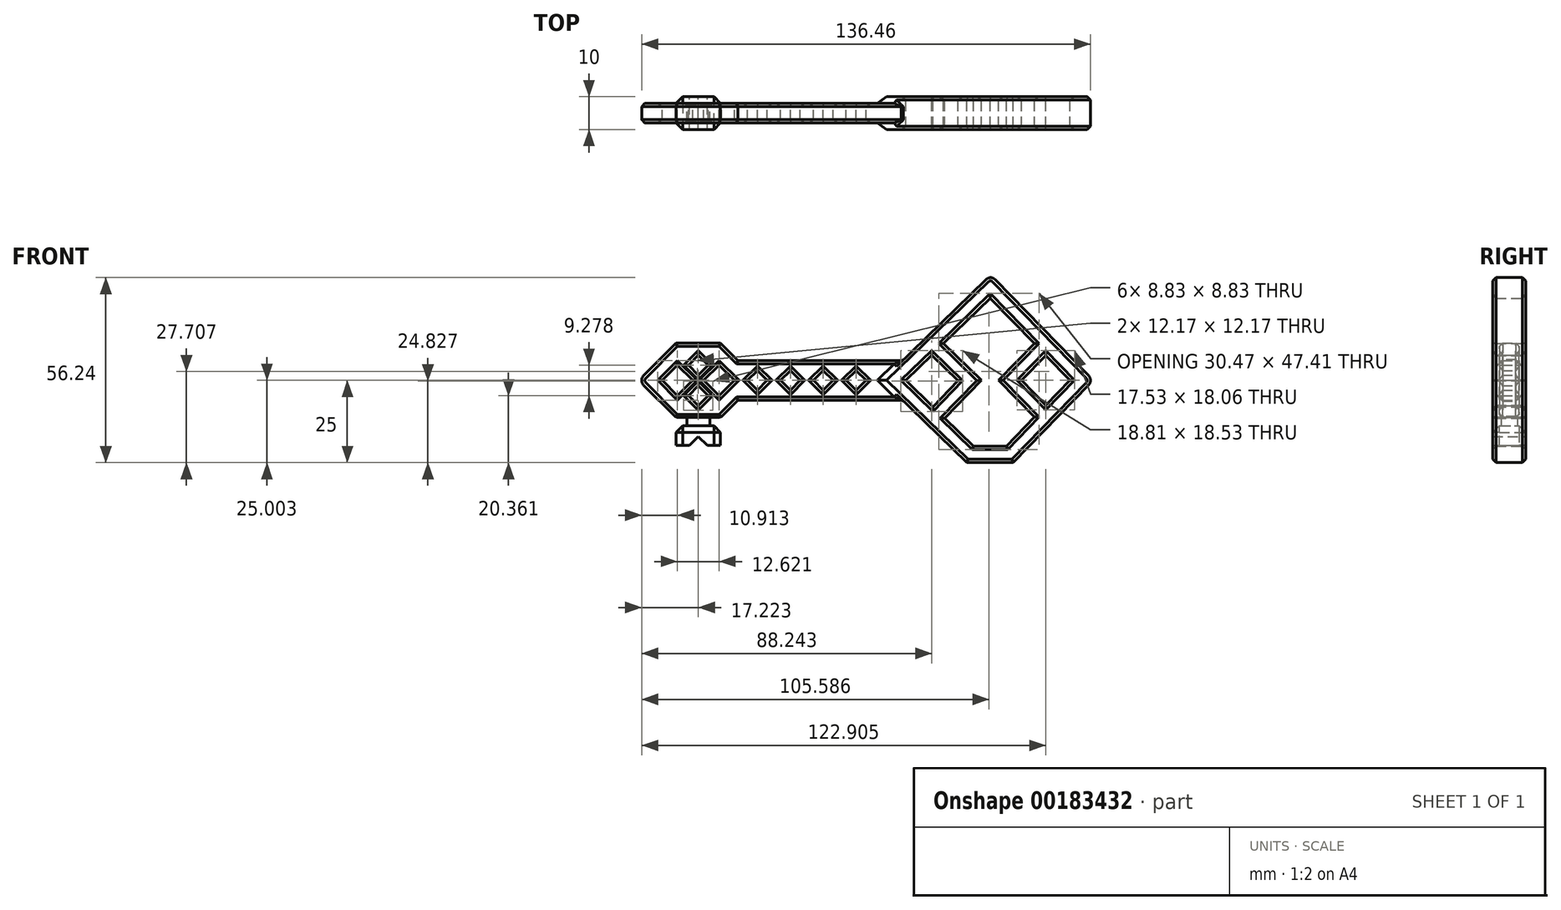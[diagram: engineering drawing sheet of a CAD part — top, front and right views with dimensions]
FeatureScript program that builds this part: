
annotation { "Feature Type Name" : "Feature", "Feature Type Description" : "" }
export const myFeature = defineFeature(function(context is Context, id is Id, definition is map)
    precondition{}
    {
        {
            var Q0;
            Q0=qCreatedBy(makeId("Front.planeOp"),FACE);
            var sketch = newSketch(context, id + "F0", { "sketchPlane" : qUnion([Q0])});
            skLineSegment(sketch, "E0", {"start": v(20.1, -6) * mm, "end": v(-29.9, -6) * mm});
            skLineSegment(sketch, "E1.MirrorCS", {"start": v(20.1, 6) * mm, "end": v(-29.9, 6) * mm});
            skLineSegment(sketch, "E2", {"start": v(71.1, 0) * mm, "end": v(63.73, 7.6) * mm});
            skLineSegment(sketch, "E3", {"start": v(46.84, 25) * mm, "end": v(32.62, 11.18) * mm});
            skLineSegment(sketch, "E4", {"start": v(21.1, 0) * mm, "end": v(29.37, -8.02) * mm});
            skLineSegment(sketch, "E5", {"start": v(51.7, -20) * mm, "end": v(60.26, -11.18) * mm});
            skLineSegment(sketch, "E6.0", {"start": v(45.51, 30.68) * mm, "end": v(13.93, 0) * mm});
            skLineSegment(sketch, "E6.1", {"start": v(76.72, 1.4) * mm, "end": v(48.34, 30.64) * mm});
            skLineSegment(sketch, "E6.2", {"start": v(53.8, -25) * mm, "end": v(76.72, -1.4) * mm});
            skLineSegment(sketch, "E6.3", {"start": v(13.93, 0) * mm, "end": v(39.67, -25) * mm});
            skLineSegment(sketch, "E7", {"start": v(41.7, -20) * mm, "end": v(51.7, -20) * mm});
            skLineSegment(sketch, "E8", {"start": v(32.95, -11.5) * mm, "end": v(44.13, 0) * mm});
            skLineSegment(sketch, "E9", {"start": v(44.13, 0) * mm, "end": v(32.62, 11.18) * mm});
            skLineSegment(sketch, "E10", {"start": v(60.25, 11.18) * mm, "end": v(49.4, 0) * mm});
            skLineSegment(sketch, "E11", {"start": v(49.4, 0) * mm, "end": v(60.26, -11.18) * mm});
            skLineSegment(sketch, "E12.0", {"start": v(37.06, -0.1) * mm, "end": v(29.03, 7.7) * mm});
            skLineSegment(sketch, "E12.1", {"start": v(29.37, -8.02) * mm, "end": v(37.06, -0.1) * mm});
            skLineSegment(sketch, "E13.0", {"start": v(56.37, 0) * mm, "end": v(63.74, -7.59) * mm});
            skLineSegment(sketch, "E13.1", {"start": v(63.73, 7.6) * mm, "end": v(56.37, 0) * mm});
            skLineSegment(sketch, "E14.trimOffspring", {"start": v(60.25, 11.18) * mm, "end": v(46.84, 25) * mm});
            skLineSegment(sketch, "E15.trimOffspring", {"start": v(63.74, -7.59) * mm, "end": v(71.1, 0) * mm});
            skLineSegment(sketch, "E16.trimOffspring", {"start": v(32.95, -11.5) * mm, "end": v(41.7, -20) * mm});
            skLineSegment(sketch, "E17.trimOffspring", {"start": v(29.03, 7.7) * mm, "end": v(21.1, 0) * mm});
            skLineSegment(sketch, "E18", {"start": v(39.67, -25) * mm, "end": v(53.8, -25) * mm});
            skPoint(sketch, "E19.orphan", {"position": v(46.84, -25) * mm});
            skPoint(sketch, "E20.visualSharp", {"position": v(46.95, 32.07) * mm});
            skArc(sketch, "E20.filletArc", {"start": v(48.34, 30.64) * mm, "mid": v(46.93, 31.24) * mm, "end": v(45.51, 30.68) * mm});
            skPoint(sketch, "E21.visualSharp", {"position": v(78.07, 0) * mm});
            skArc(sketch, "E21.filletArc", {"start": v(76.72, -1.4) * mm, "mid": v(77.29, 0) * mm, "end": v(76.72, 1.4) * mm});
            skLineSegment(sketch, "E22", {"start": v(-35.2, 11.31) * mm, "end": v(-48.69, 11.31) * mm});
            skLineSegment(sketch, "E23", {"start": v(-48.69, 11.31) * mm, "end": v(-58.59, 1.41) * mm});
            skLineSegment(sketch, "E24", {"start": v(-29.9, 6) * mm, "end": v(-35.2, 11.31) * mm});
            skLineSegment(sketch, "E25", {"start": v(-29.9, -6) * mm, "end": v(-35.2, -11.31) * mm});
            skLineSegment(sketch, "E26", {"start": v(-35.2, -11.31) * mm, "end": v(-48.69, -11.31) * mm});
            skLineSegment(sketch, "E27", {"start": v(-48.69, -11.31) * mm, "end": v(-58.59, -1.41) * mm});
            skLineSegment(sketch, "E28", {"start": v(-45.45, -11.31) * mm, "end": v(-45.45, -13.81) * mm});
            skLineSegment(sketch, "E29", {"start": v(-41.95, -11.31) * mm, "end": v(-41.95, -29.27) * mm, "construction": true});
            skLineSegment(sketch, "E30", {"start": v(-41.95, -13.81) * mm, "end": v(-48.69, -13.81) * mm});
            skLineSegment(sketch, "E31", {"start": v(-48.69, -13.81) * mm, "end": v(-48.69, -19.81) * mm});
            skLineSegment(sketch, "E32", {"start": v(-48.69, -19.81) * mm, "end": v(-44.69, -19.81) * mm});
            skLineSegment(sketch, "E33", {"start": v(-44.69, -19.81) * mm, "end": v(-41.95, -17.07) * mm});
            skLineSegment(sketch, "E34.MirrorCS", {"start": v(-38.45, -11.31) * mm, "end": v(-38.45, -13.81) * mm});
            skLineSegment(sketch, "E35.MirrorCS", {"start": v(-41.95, -13.81) * mm, "end": v(-35.2, -13.81) * mm});
            skLineSegment(sketch, "E36.MirrorCS", {"start": v(-35.2, -13.81) * mm, "end": v(-35.2, -19.81) * mm});
            skLineSegment(sketch, "E37.MirrorCS", {"start": v(-35.2, -19.81) * mm, "end": v(-39.2, -19.81) * mm});
            skLineSegment(sketch, "E38.MirrorCS", {"start": v(-39.2, -19.81) * mm, "end": v(-41.95, -17.07) * mm});
            skLineSegment(sketch, "E39.0", {"start": v(-33.43, -2.46) * mm, "end": v(-35.64, -4.67) * mm});
            skLineSegment(sketch, "E39.2", {"start": v(-33.43, 2.46) * mm, "end": v(-35.64, 4.67) * mm});
            skLineSegment(sketch, "E39.4", {"start": v(-48.26, 4.67) * mm, "end": v(-52.93, 0) * mm});
            skLineSegment(sketch, "E39.5", {"start": v(-48.26, -4.67) * mm, "end": v(-52.93, 0) * mm});
            skLineSegment(sketch, "E40.trimOffspring", {"start": v(-43.59, 0) * mm, "end": v(-48.26, -4.67) * mm});
            skLineSegment(sketch, "E41.trimOffspring", {"start": v(-43.59, 0) * mm, "end": v(-48.26, 4.67) * mm});
            skLineSegment(sketch, "E42.trimOffspring", {"start": v(-40.3, 0) * mm, "end": v(-35.64, 4.67) * mm});
            skLineSegment(sketch, "E43.trimOffspring", {"start": v(-40.3, 0) * mm, "end": v(-35.64, -4.67) * mm});
            skLineSegment(sketch, "E44", {"start": v(-33.43, 2.46) * mm, "end": v(-30.96, 0) * mm});
            skLineSegment(sketch, "E45", {"start": v(-30.96, 0) * mm, "end": v(-33.43, -2.46) * mm});
            skPoint(sketch, "E46.visualSharp", {"position": v(-60, 0) * mm});
            skArc(sketch, "E46.filletArc", {"start": v(-58.59, 1.41) * mm, "mid": v(-59.17, 0) * mm, "end": v(-58.59, -1.41) * mm});
            skLineSegment(sketch, "E47", {"start": v(-26.96, 0) * mm, "end": v(-23.96, 3) * mm});
            skLineSegment(sketch, "E48", {"start": v(-23.96, 3) * mm, "end": v(-20.96, 0) * mm});
            skLineSegment(sketch, "E49.1.0.0", {"start": v(-16.96, 0) * mm, "end": v(-13.96, 3) * mm});
            skLineSegment(sketch, "E49.1.0.1", {"start": v(-13.96, 3) * mm, "end": v(-10.96, 0) * mm});
            skLineSegment(sketch, "E49.2.0.0", {"start": v(-6.96, 0) * mm, "end": v(-3.96, 3) * mm});
            skLineSegment(sketch, "E49.2.0.1", {"start": v(-3.96, 3) * mm, "end": v(-0.96, 0) * mm});
            skLineSegment(sketch, "E49.3.0.0", {"start": v(3.04, 0) * mm, "end": v(6.04, 3) * mm});
            skLineSegment(sketch, "E49.3.0.1", {"start": v(6.04, 3) * mm, "end": v(9.04, 0) * mm});
            skLineSegment(sketch, "E49.direction1", {"start": v(-26.96, 0) * mm, "end": v(-16.96, 0) * mm, "construction": true});
            skLineSegment(sketch, "E50.MirrorCS", {"start": v(-26.96, 0) * mm, "end": v(-23.96, -3) * mm});
            skLineSegment(sketch, "E51.MirrorCS", {"start": v(-23.96, -3) * mm, "end": v(-20.96, 0) * mm});
            skLineSegment(sketch, "E52.MirrorCS", {"start": v(-16.96, 0) * mm, "end": v(-13.96, -3) * mm});
            skLineSegment(sketch, "E53.MirrorCS", {"start": v(-13.96, -3) * mm, "end": v(-10.96, 0) * mm});
            skLineSegment(sketch, "E54.MirrorCS", {"start": v(-6.96, 0) * mm, "end": v(-3.96, -3) * mm});
            skLineSegment(sketch, "E55.MirrorCS", {"start": v(-3.96, -3) * mm, "end": v(-0.96, 0) * mm});
            skLineSegment(sketch, "E56.MirrorCS", {"start": v(3.04, 0) * mm, "end": v(6.04, -3) * mm});
            skLineSegment(sketch, "E57.MirrorCS", {"start": v(6.04, -3) * mm, "end": v(9.04, 0) * mm});
            skLineSegment(sketch, "E58.1.0.0", {"start": v(-44.95, -4.64) * mm, "end": v(-41.95, -1.64) * mm});
            skLineSegment(sketch, "E58.1.0.1", {"start": v(-41.95, -1.64) * mm, "end": v(-38.95, -4.64) * mm});
            skLineSegment(sketch, "E59.MirrorCS", {"start": v(-44.95, -4.64) * mm, "end": v(-41.95, -7.64) * mm});
            skLineSegment(sketch, "E60.MirrorCS", {"start": v(-41.95, -7.64) * mm, "end": v(-38.95, -4.64) * mm});
            skLineSegment(sketch, "E61", {"start": v(-41.95, 20.91) * mm, "end": v(-41.95, -13.81) * mm, "construction": true});
            skLineSegment(sketch, "E62.MirrorCS", {"start": v(-44.95, 4.64) * mm, "end": v(-41.95, 1.64) * mm});
            skLineSegment(sketch, "E63.MirrorCS", {"start": v(-41.95, 1.64) * mm, "end": v(-38.95, 4.64) * mm});
            skLineSegment(sketch, "E64.MirrorCS", {"start": v(-41.95, 7.64) * mm, "end": v(-38.95, 4.64) * mm});
            skLineSegment(sketch, "E65.MirrorCS", {"start": v(-44.95, 4.64) * mm, "end": v(-41.95, 7.64) * mm});
            skSolve(sketch);
        }
        {
            var Q0;
            Q0=makeQuery(id+"F0.imprint","IMPRINT",FACE,{"disambiguationData":[TD([[makeQuery(id+"F0.imprint","IMPRINT",EDGE,{"derivedFrom":sQuery(id+"F0.wireOp",EDGE,"E2")}),-1.0]])]});
            var Q1;
            {var subQ0=sQuery(id+"F0.wireOp",EDGE,"E31");Q1=makeQuery(id+"F0.imprint","IMPRINT",FACE,{"disambiguationData":[TD([[makeQuery(id+"F0.imprint","IMPRINT",EDGE,{"derivedFrom":subQ0}),1.0]])]});}
            extrude(context, id + "F1", {"entities" : qUnion([Q0, Q1]), "endBound" : BoundingType.SYMMETRIC, "depth" : 10 * mm});
        }
        {
            var Q0;
            {var subQ4=sQuery(id+"F0.wireOp",EDGE,"E0");Q0=makeQuery(id+"F0.imprint","IMPRINT",FACE,{"disambiguationData":[TD([[makeQuery(id+"F0.imprint","IMPRINT",EDGE,{"derivedFrom":subQ4}),-1.0]])]});}
            var Q1;
            Q1=makeQuery(id+"F0.imprint","IMPRINT",FACE,{"disambiguationData":[TD([[makeQuery(id+"F0.imprint","IMPRINT",EDGE,{"derivedFrom":sQuery(id+"F0.wireOp",EDGE,"E39.3")}),1.0]])]});
            var Q2;
            Q2=makeQuery(id+"F0.imprint","IMPRINT",FACE,{"disambiguationData":[TD([[makeQuery(id+"F0.imprint","IMPRINT",EDGE,{"derivedFrom":sQuery(id+"F0.wireOp",EDGE,"E39.1")}),-1.0]])]});
            extrude(context, id + "F2", {"entities" : qUnion([Q0, Q1, Q2]), "operationType" : NewBodyOperationType.ADD, "endBound" : BoundingType.SYMMETRIC, "depth" : 6 * mm});
        }
        {
            var Q0;
            {var subQ2=sQuery(id+"F0.wireOp",EDGE,"E28");Q0=makeQuery(id+"F0.imprint","IMPRINT",FACE,{"disambiguationData":[TD([[makeQuery(id+"F0.imprint","IMPRINT",EDGE,{"derivedFrom":subQ2}),1.0]])]});}
            extrude(context, id + "F3", {"entities" : qUnion([Q0]), "endBound" : BoundingType.SYMMETRIC, "depth" : 5 * mm});
        }
        {
            var Q0;
            Q0=makeQuery(id+"F2.opExtrude","CAP_EDGE",EDGE,{"disambiguationData":[OSD([sQuery(id+"F0.wireOp",EDGE,"E47")])],"isStart":false});
            var Q1;
            Q1=makeQuery(id+"F2.opExtrude","CAP_EDGE",EDGE,{"disambiguationData":[OSD([sQuery(id+"F0.wireOp",EDGE,"E48")])],"isStart":false});
            var Q2;
            Q2=makeQuery(id+"F2.opExtrude","CAP_EDGE",EDGE,{"disambiguationData":[OSD([sQuery(id+"F0.wireOp",EDGE,"E51.MirrorCS")])],"isStart":false});
            var Q3;
            Q3=makeQuery(id+"F2.opExtrude","CAP_EDGE",EDGE,{"disambiguationData":[OSD([sQuery(id+"F0.wireOp",EDGE,"E50.MirrorCS")])],"isStart":false});
            var Q4;
            Q4=makeQuery(id+"F2.opExtrude","CAP_EDGE",EDGE,{"disambiguationData":[OSD([sQuery(id+"F0.wireOp",EDGE,"E49.1.0.0")])],"isStart":false});
            var Q5;
            Q5=makeQuery(id+"F2.opExtrude","CAP_EDGE",EDGE,{"disambiguationData":[OSD([sQuery(id+"F0.wireOp",EDGE,"E49.1.0.1")])],"isStart":false});
            var Q6;
            Q6=makeQuery(id+"F2.opExtrude","CAP_EDGE",EDGE,{"disambiguationData":[OSD([sQuery(id+"F0.wireOp",EDGE,"E53.MirrorCS")])],"isStart":false});
            var Q7;
            Q7=makeQuery(id+"F2.opExtrude","CAP_FACE",FACE,{"disambiguationData":[OSD([sQuery(id+"F0.wireOp",EDGE,"E0"),sQuery(id+"F0.wireOp",EDGE,"E1.MirrorCS"),sQuery(id+"F0.wireOp",EDGE,"E6.0"),sQuery(id+"F0.wireOp",EDGE,"E6.3"),sQuery(id+"F0.wireOp",EDGE,"E22"),sQuery(id+"F0.wireOp",EDGE,"E23"),sQuery(id+"F0.wireOp",EDGE,"E24"),sQuery(id+"F0.wireOp",EDGE,"E25"),sQuery(id+"F0.wireOp",EDGE,"E26"),sQuery(id+"F0.wireOp",EDGE,"E27"),sQuery(id+"F0.wireOp",EDGE,"E39.0"),sQuery(id+"F0.wireOp",EDGE,"E39.1"),sQuery(id+"F0.wireOp",EDGE,"E39.2"),sQuery(id+"F0.wireOp",EDGE,"E39.3"),sQuery(id+"F0.wireOp",EDGE,"E39.4"),sQuery(id+"F0.wireOp",EDGE,"E39.5"),sQuery(id+"F0.wireOp",EDGE,"SuCAYquI-ejI9-Igzf-Qkme-vMYG3JWezhbn"),sQuery(id+"F0.wireOp",EDGE,"5v7E9WHn-bbCv-sJz2-O0Js-mJgPAPqvvkll"),sQuery(id+"F0.wireOp",EDGE,"vqwsvxok-3IlO-Vk3z-uLZy-tBUQALx8QQG8"),sQuery(id+"F0.wireOp",EDGE,"VJvgWDCh-3OEa-ATRK-sCer-f1ydQRvW1O1d"),sQuery(id+"F0.wireOp",EDGE,"E40.trimOffspring"),sQuery(id+"F0.wireOp",EDGE,"E41.trimOffspring"),sQuery(id+"F0.wireOp",EDGE,"E42.trimOffspring"),sQuery(id+"F0.wireOp",EDGE,"E43.trimOffspring"),sQuery(id+"F0.wireOp",EDGE,"E44"),sQuery(id+"F0.wireOp",EDGE,"E45"),sQuery(id+"F0.wireOp",EDGE,"E46.filletArc"),sQuery(id+"F0.wireOp",EDGE,"E47"),sQuery(id+"F0.wireOp",EDGE,"E48"),sQuery(id+"F0.wireOp",EDGE,"E49.1.0.0"),sQuery(id+"F0.wireOp",EDGE,"E49.1.0.1"),sQuery(id+"F0.wireOp",EDGE,"E49.2.0.0"),sQuery(id+"F0.wireOp",EDGE,"E49.2.0.1"),sQuery(id+"F0.wireOp",EDGE,"E49.3.0.0"),sQuery(id+"F0.wireOp",EDGE,"E49.3.0.1"),sQuery(id+"F0.wireOp",EDGE,"E50.MirrorCS"),sQuery(id+"F0.wireOp",EDGE,"E51.MirrorCS"),sQuery(id+"F0.wireOp",EDGE,"E52.MirrorCS"),sQuery(id+"F0.wireOp",EDGE,"E53.MirrorCS"),sQuery(id+"F0.wireOp",EDGE,"E54.MirrorCS"),sQuery(id+"F0.wireOp",EDGE,"E55.MirrorCS"),sQuery(id+"F0.wireOp",EDGE,"E56.MirrorCS"),sQuery(id+"F0.wireOp",EDGE,"E57.MirrorCS")])],"isStart":false});
            var Q8;
            Q8=makeQuery(id+"F2.opExtrude","CAP_FACE",FACE,{"disambiguationData":[OSD([sQuery(id+"F0.wireOp",EDGE,"E0"),sQuery(id+"F0.wireOp",EDGE,"E1.MirrorCS"),sQuery(id+"F0.wireOp",EDGE,"E6.0"),sQuery(id+"F0.wireOp",EDGE,"E6.3"),sQuery(id+"F0.wireOp",EDGE,"E22"),sQuery(id+"F0.wireOp",EDGE,"E23"),sQuery(id+"F0.wireOp",EDGE,"E24"),sQuery(id+"F0.wireOp",EDGE,"E25"),sQuery(id+"F0.wireOp",EDGE,"E26"),sQuery(id+"F0.wireOp",EDGE,"E27"),sQuery(id+"F0.wireOp",EDGE,"E39.0"),sQuery(id+"F0.wireOp",EDGE,"E39.1"),sQuery(id+"F0.wireOp",EDGE,"E39.2"),sQuery(id+"F0.wireOp",EDGE,"E39.3"),sQuery(id+"F0.wireOp",EDGE,"E39.4"),sQuery(id+"F0.wireOp",EDGE,"E39.5"),sQuery(id+"F0.wireOp",EDGE,"SuCAYquI-ejI9-Igzf-Qkme-vMYG3JWezhbn"),sQuery(id+"F0.wireOp",EDGE,"5v7E9WHn-bbCv-sJz2-O0Js-mJgPAPqvvkll"),sQuery(id+"F0.wireOp",EDGE,"vqwsvxok-3IlO-Vk3z-uLZy-tBUQALx8QQG8"),sQuery(id+"F0.wireOp",EDGE,"VJvgWDCh-3OEa-ATRK-sCer-f1ydQRvW1O1d"),sQuery(id+"F0.wireOp",EDGE,"E40.trimOffspring"),sQuery(id+"F0.wireOp",EDGE,"E41.trimOffspring"),sQuery(id+"F0.wireOp",EDGE,"E42.trimOffspring"),sQuery(id+"F0.wireOp",EDGE,"E43.trimOffspring"),sQuery(id+"F0.wireOp",EDGE,"E44"),sQuery(id+"F0.wireOp",EDGE,"E45"),sQuery(id+"F0.wireOp",EDGE,"E46.filletArc"),sQuery(id+"F0.wireOp",EDGE,"E47"),sQuery(id+"F0.wireOp",EDGE,"E48"),sQuery(id+"F0.wireOp",EDGE,"E49.1.0.0"),sQuery(id+"F0.wireOp",EDGE,"E49.1.0.1"),sQuery(id+"F0.wireOp",EDGE,"E49.2.0.0"),sQuery(id+"F0.wireOp",EDGE,"E49.2.0.1"),sQuery(id+"F0.wireOp",EDGE,"E49.3.0.0"),sQuery(id+"F0.wireOp",EDGE,"E49.3.0.1"),sQuery(id+"F0.wireOp",EDGE,"E50.MirrorCS"),sQuery(id+"F0.wireOp",EDGE,"E51.MirrorCS"),sQuery(id+"F0.wireOp",EDGE,"E52.MirrorCS"),sQuery(id+"F0.wireOp",EDGE,"E53.MirrorCS"),sQuery(id+"F0.wireOp",EDGE,"E54.MirrorCS"),sQuery(id+"F0.wireOp",EDGE,"E55.MirrorCS"),sQuery(id+"F0.wireOp",EDGE,"E56.MirrorCS"),sQuery(id+"F0.wireOp",EDGE,"E57.MirrorCS")])],"isStart":true});
            var Q9;
            Q9=makeQuery(id+"F2.opExtrude","SWEPT_EDGE",EDGE,{"disambiguationData":[OSD([sQuery(id+"F0.wireOp",EDGE,"E26"),sQuery(id+"F0.wireOp",EDGE,"E27")])]});
            var Q10;
            Q10=makeQuery(id+"F2.opExtrude","SWEPT_EDGE",EDGE,{"disambiguationData":[OSD([sQuery(id+"F0.wireOp",EDGE,"E25"),sQuery(id+"F0.wireOp",EDGE,"E26")])]});
            chamfer(context, id + "F4", {"entities" : qUnion([Q0, Q1, Q2, Q3, Q4, Q5, Q6, Q7, Q8, Q9, Q10]), "width" : 1 * mm, "tangentPropagation" : true});
        }
        {
            var Q0;
            Q0=makeQuery(id+"F1.opExtrude","CAP_EDGE",EDGE,{"disambiguationData":[OSD([sQuery(id+"F0.wireOp",EDGE,"E30"),sQuery(id+"F0.wireOp",EDGE,"E35.MirrorCS")])],"isStart":false});
            var Q1;
            Q1=makeQuery(id+"F1.opExtrude","SWEPT_EDGE",EDGE,{"disambiguationData":[OSD([sQuery(id+"F0.wireOp",EDGE,"E30"),sQuery(id+"F0.wireOp",EDGE,"E31")])]});
            var Q2;
            Q2=makeQuery(id+"F1.opExtrude","SWEPT_EDGE",EDGE,{"disambiguationData":[OSD([sQuery(id+"F0.wireOp",EDGE,"E35.MirrorCS"),sQuery(id+"F0.wireOp",EDGE,"E36.MirrorCS")])]});
            var Q3;
            Q3=makeQuery(id+"F1.opExtrude","CAP_EDGE",EDGE,{"disambiguationData":[OSD([sQuery(id+"F0.wireOp",EDGE,"E30"),sQuery(id+"F0.wireOp",EDGE,"E35.MirrorCS")])],"isStart":true});
            var Q4;
            Q4=makeQuery(id+"F1.opExtrude","CAP_EDGE",EDGE,{"disambiguationData":[OSD([sQuery(id+"F0.wireOp",EDGE,"E31")])],"isStart":false});
            var Q5;
            Q5=makeQuery(id+"F1.opExtrude","CAP_EDGE",EDGE,{"disambiguationData":[OSD([sQuery(id+"F0.wireOp",EDGE,"E36.MirrorCS")])],"isStart":false});
            var Q6;
            Q6=makeQuery(id+"F1.opExtrude","CAP_EDGE",EDGE,{"disambiguationData":[OSD([sQuery(id+"F0.wireOp",EDGE,"E31")])],"isStart":true});
            var Q7;
            Q7=makeQuery(id+"F1.opExtrude","CAP_EDGE",EDGE,{"disambiguationData":[OSD([sQuery(id+"F0.wireOp",EDGE,"E36.MirrorCS")])],"isStart":true});
            chamfer(context, id + "F5", {"entities" : qUnion([Q0, Q1, Q2, Q3, Q4, Q5, Q6, Q7]), "width" : 2 * mm, "tangentPropagation" : true});
        }
        {
            var Q0;
            Q0=makeQuery(id+"F1.opExtrude","CAP_EDGE",EDGE,{"disambiguationData":[OSD([sQuery(id+"F0.wireOp",EDGE,"E12.0")])],"isStart":false});
            var Q1;
            Q1=makeQuery(id+"F1.opExtrude","CAP_EDGE",EDGE,{"disambiguationData":[OSD([sQuery(id+"F0.wireOp",EDGE,"E12.1")])],"isStart":false});
            var Q2;
            Q2=makeQuery(id+"F1.opExtrude","CAP_EDGE",EDGE,{"disambiguationData":[OSD([sQuery(id+"F0.wireOp",EDGE,"E17.trimOffspring")])],"isStart":false});
            var Q3;
            Q3=makeQuery(id+"F1.opExtrude","CAP_EDGE",EDGE,{"disambiguationData":[OSD([sQuery(id+"F0.wireOp",EDGE,"E4")])],"isStart":false});
            var Q4;
            Q4=makeQuery(id+"F1.opExtrude","CAP_EDGE",EDGE,{"disambiguationData":[OSD([sQuery(id+"F0.wireOp",EDGE,"E12.0")])],"isStart":true});
            var Q5;
            Q5=makeQuery(id+"F1.opExtrude","CAP_EDGE",EDGE,{"disambiguationData":[OSD([sQuery(id+"F0.wireOp",EDGE,"E17.trimOffspring")])],"isStart":true});
            var Q6;
            Q6=makeQuery(id+"F1.opExtrude","CAP_EDGE",EDGE,{"disambiguationData":[OSD([sQuery(id+"F0.wireOp",EDGE,"E12.1")])],"isStart":true});
            var Q7;
            Q7=makeQuery(id+"F1.opExtrude","CAP_EDGE",EDGE,{"disambiguationData":[OSD([sQuery(id+"F0.wireOp",EDGE,"E4")])],"isStart":true});
            var Q8;
            Q8=makeQuery(id+"F1.opExtrude","CAP_EDGE",EDGE,{"disambiguationData":[OSD([sQuery(id+"F0.wireOp",EDGE,"E13.0")])],"isStart":true});
            var Q9;
            Q9=makeQuery(id+"F1.opExtrude","CAP_EDGE",EDGE,{"disambiguationData":[OSD([sQuery(id+"F0.wireOp",EDGE,"E13.1")])],"isStart":true});
            var Q10;
            Q10=makeQuery(id+"F1.opExtrude","CAP_EDGE",EDGE,{"disambiguationData":[OSD([sQuery(id+"F0.wireOp",EDGE,"E2")])],"isStart":true});
            var Q11;
            Q11=makeQuery(id+"F1.opExtrude","CAP_EDGE",EDGE,{"disambiguationData":[OSD([sQuery(id+"F0.wireOp",EDGE,"E15.trimOffspring")])],"isStart":true});
            var Q12;
            Q12=makeQuery(id+"F1.opExtrude","CAP_EDGE",EDGE,{"disambiguationData":[OSD([sQuery(id+"F0.wireOp",EDGE,"E15.trimOffspring")])],"isStart":false});
            var Q13;
            Q13=makeQuery(id+"F1.opExtrude","CAP_EDGE",EDGE,{"disambiguationData":[OSD([sQuery(id+"F0.wireOp",EDGE,"E2")])],"isStart":false});
            var Q14;
            Q14=makeQuery(id+"F1.opExtrude","CAP_EDGE",EDGE,{"disambiguationData":[OSD([sQuery(id+"F0.wireOp",EDGE,"E13.1")])],"isStart":false});
            var Q15;
            Q15=makeQuery(id+"F1.opExtrude","CAP_EDGE",EDGE,{"disambiguationData":[OSD([sQuery(id+"F0.wireOp",EDGE,"E13.0")])],"isStart":false});
            var Q16;
            Q16=makeQuery(id+"F1.opExtrude","CAP_EDGE",EDGE,{"disambiguationData":[OSD([sQuery(id+"F0.wireOp",EDGE,"E3")])],"isStart":false});
            var Q17;
            Q17=makeQuery(id+"F1.opExtrude","CAP_EDGE",EDGE,{"disambiguationData":[OSD([sQuery(id+"F0.wireOp",EDGE,"E14.trimOffspring")])],"isStart":false});
            var Q18;
            Q18=makeQuery(id+"F1.opExtrude","CAP_EDGE",EDGE,{"disambiguationData":[OSD([sQuery(id+"F0.wireOp",EDGE,"E10")])],"isStart":false});
            var Q19;
            Q19=makeQuery(id+"F1.opExtrude","CAP_EDGE",EDGE,{"disambiguationData":[OSD([sQuery(id+"F0.wireOp",EDGE,"E11")])],"isStart":false});
            var Q20;
            Q20=makeQuery(id+"F1.opExtrude","CAP_EDGE",EDGE,{"disambiguationData":[OSD([sQuery(id+"F0.wireOp",EDGE,"E5")])],"isStart":false});
            var Q21;
            Q21=makeQuery(id+"F1.opExtrude","CAP_FACE",FACE,{"disambiguationData":[OSD([sQuery(id+"F0.wireOp",EDGE,"E2"),sQuery(id+"F0.wireOp",EDGE,"E3"),sQuery(id+"F0.wireOp",EDGE,"E4"),sQuery(id+"F0.wireOp",EDGE,"E5"),sQuery(id+"F0.wireOp",EDGE,"E6.0"),sQuery(id+"F0.wireOp",EDGE,"E6.1"),sQuery(id+"F0.wireOp",EDGE,"E6.2"),sQuery(id+"F0.wireOp",EDGE,"E6.3"),sQuery(id+"F0.wireOp",EDGE,"E7"),sQuery(id+"F0.wireOp",EDGE,"E8"),sQuery(id+"F0.wireOp",EDGE,"E9"),sQuery(id+"F0.wireOp",EDGE,"E10"),sQuery(id+"F0.wireOp",EDGE,"E11"),sQuery(id+"F0.wireOp",EDGE,"E12.0"),sQuery(id+"F0.wireOp",EDGE,"E12.1"),sQuery(id+"F0.wireOp",EDGE,"E13.0"),sQuery(id+"F0.wireOp",EDGE,"E13.1"),sQuery(id+"F0.wireOp",EDGE,"E14.trimOffspring"),sQuery(id+"F0.wireOp",EDGE,"E15.trimOffspring"),sQuery(id+"F0.wireOp",EDGE,"E16.trimOffspring"),sQuery(id+"F0.wireOp",EDGE,"E17.trimOffspring"),sQuery(id+"F0.wireOp",EDGE,"E18"),sQuery(id+"F0.wireOp",EDGE,"E20.filletArc"),sQuery(id+"F0.wireOp",EDGE,"E21.filletArc")])],"isStart":false});
            var Q22;
            Q22=makeQuery(id+"F1.opExtrude","CAP_FACE",FACE,{"disambiguationData":[OSD([sQuery(id+"F0.wireOp",EDGE,"E2"),sQuery(id+"F0.wireOp",EDGE,"E3"),sQuery(id+"F0.wireOp",EDGE,"E4"),sQuery(id+"F0.wireOp",EDGE,"E5"),sQuery(id+"F0.wireOp",EDGE,"E6.0"),sQuery(id+"F0.wireOp",EDGE,"E6.1"),sQuery(id+"F0.wireOp",EDGE,"E6.2"),sQuery(id+"F0.wireOp",EDGE,"E6.3"),sQuery(id+"F0.wireOp",EDGE,"E7"),sQuery(id+"F0.wireOp",EDGE,"E8"),sQuery(id+"F0.wireOp",EDGE,"E9"),sQuery(id+"F0.wireOp",EDGE,"E10"),sQuery(id+"F0.wireOp",EDGE,"E11"),sQuery(id+"F0.wireOp",EDGE,"E12.0"),sQuery(id+"F0.wireOp",EDGE,"E12.1"),sQuery(id+"F0.wireOp",EDGE,"E13.0"),sQuery(id+"F0.wireOp",EDGE,"E13.1"),sQuery(id+"F0.wireOp",EDGE,"E14.trimOffspring"),sQuery(id+"F0.wireOp",EDGE,"E15.trimOffspring"),sQuery(id+"F0.wireOp",EDGE,"E16.trimOffspring"),sQuery(id+"F0.wireOp",EDGE,"E17.trimOffspring"),sQuery(id+"F0.wireOp",EDGE,"E18"),sQuery(id+"F0.wireOp",EDGE,"E20.filletArc"),sQuery(id+"F0.wireOp",EDGE,"E21.filletArc")])],"isStart":true});
            chamfer(context, id + "F6", {"entities" : qUnion([Q0, Q1, Q2, Q3, Q4, Q5, Q6, Q7, Q8, Q9, Q10, Q11, Q12, Q13, Q14, Q15, Q16, Q17, Q18, Q19, Q20, Q21, Q22]), "width" : 1 * mm, "tangentPropagation" : true});
        }
    });
